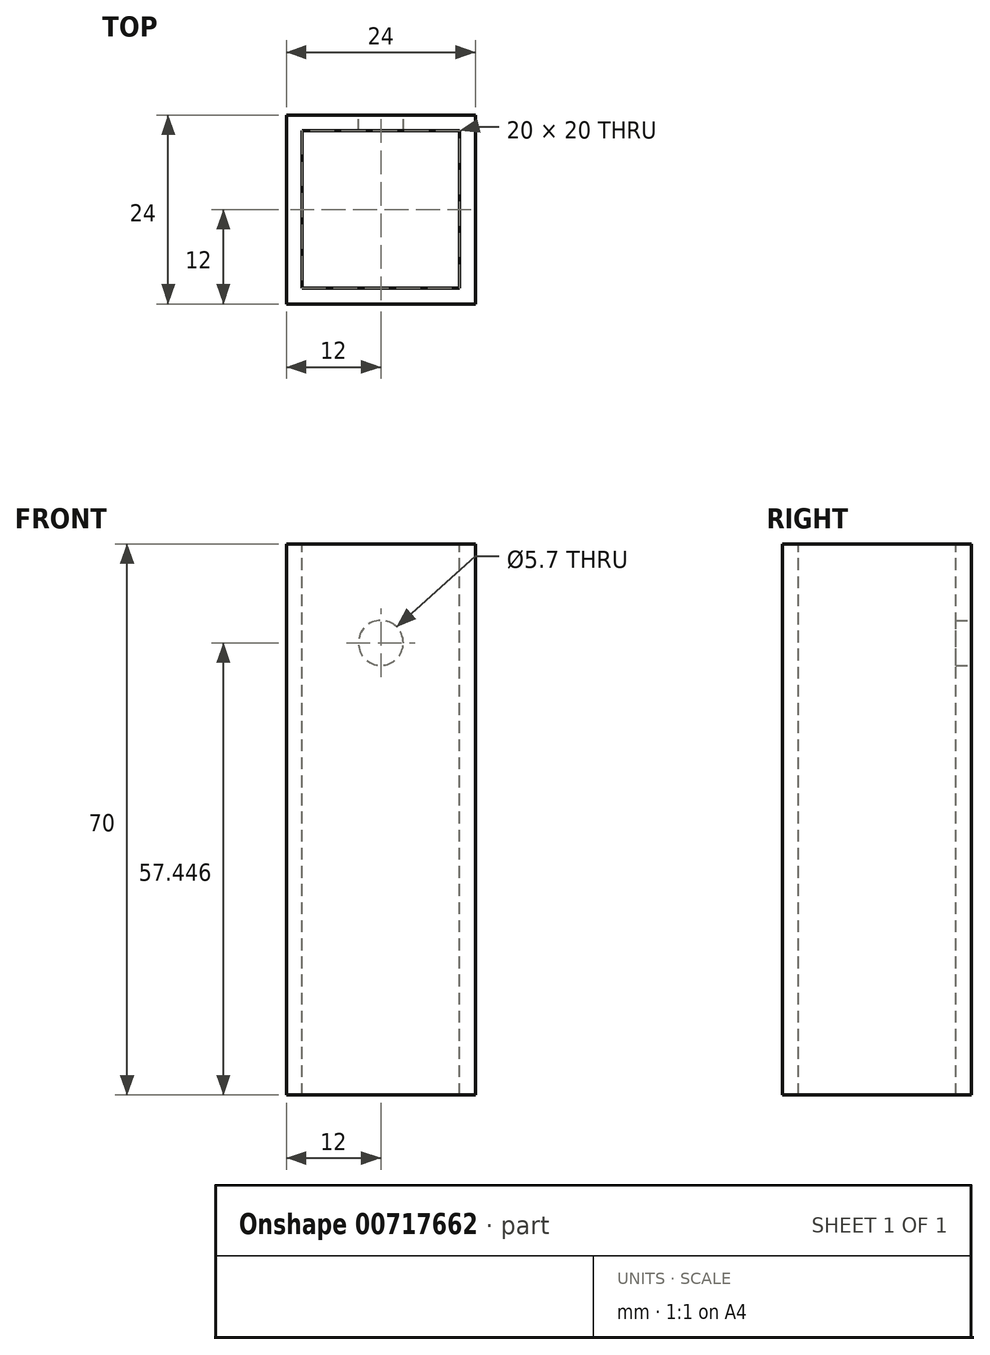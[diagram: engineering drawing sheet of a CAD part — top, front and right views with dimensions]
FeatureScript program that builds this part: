
annotation { "Feature Type Name" : "Feature", "Feature Type Description" : "" }
export const myFeature = defineFeature(function(context is Context, id is Id, definition is map)
    precondition{}
    {
        {
            var Q0;
            Q0=qCreatedBy(makeId("Front.planeOp"),FACE);
            var sketch = newSketch(context, id + "F0", { "sketchPlane" : qUnion([Q0])});
            skLineSegment(sketch, "E0.bottom", {"start": v(0, 0) * mm, "end": v(24, 0) * mm});
            skLineSegment(sketch, "E0.top", {"start": v(0, 70) * mm, "end": v(24, 70) * mm});
            skLineSegment(sketch, "E0.left", {"start": v(0, 0) * mm, "end": v(0, 70) * mm});
            skLineSegment(sketch, "E0.right", {"start": v(24, 0) * mm, "end": v(24, 70) * mm});
            skSolve(sketch);
        }
        {
            var Q0;
            Q0 = qSketchRegion(id + "F0", true);
            extrude(context, id + "F1", {"entities" : qUnion([Q0]), "depth" : 24 * mm, "offsetDistance" : 25 * mm});
        }
        {
            var Q0;
            Q0=makeQuery(id+"F1.opExtrude","SWEPT_FACE",FACE,{"disambiguationData":[OSD([sQuery(id+"F0.wireOp",EDGE,"E0.top")])]});
            var Q1;
            Q1=makeQuery(id+"F1.opExtrude","SWEPT_FACE",FACE,{"disambiguationData":[OSD([sQuery(id+"F0.wireOp",EDGE,"E0.bottom")])]});
            shell(context, id + "F2", {"entities" : qUnion([Q0, Q1]), "thickness" : 2 * mm});
        }
        {
            var Q0;
            Q0=qCreatedBy(makeId("Front.planeOp"),FACE);
            var sketch = newSketch(context, id + "F3", { "sketchPlane" : qUnion([Q0])});
            skCircle(sketch, "E1", {"center": v(12, 57.45) * mm, "radius": 2.85 * mm});
            skSolve(sketch);
        }
        {
            var Q0;
            Q0 = qSketchRegion(id + "F3", true);
            extrude(context, id + "F4", {"entities" : qUnion([Q0]), "operationType" : NewBodyOperationType.REMOVE, "depth" : 3 * mm, "offsetDistance" : 25 * mm});
        }
    });
